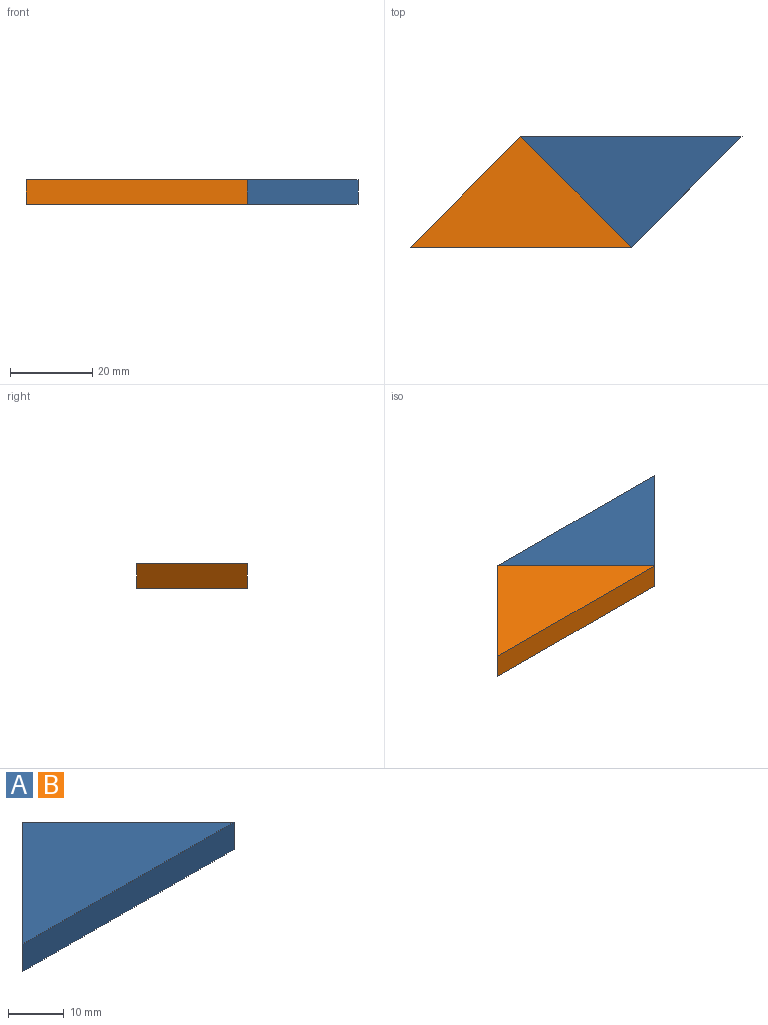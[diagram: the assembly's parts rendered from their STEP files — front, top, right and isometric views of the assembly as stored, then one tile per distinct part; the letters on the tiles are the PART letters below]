
ASSEMBLY  parts=2 mates=1
PART A: 5 faces, bbox 53.7x26.9x6 mm
  f0: plane 26.87x26.87mm, normal (-0.71,0.71,0), area 228mm2, adj f1,f2,f3,f4
  f1: plane 53.74x6mm, normal (0,-1,0), area 322.4mm2, adj f0,f2,f3,f4
  f2: plane 26.87x26.87mm, normal (0.71,0.71,0), area 228mm2, adj f0,f1,f3,f4
  f3: plane 53.74x26.87mm, normal (0,0,1), area 722mm2, adj f0,f1,f2
  f4: plane 53.74x26.87mm, normal (0,0,-1), area 722mm2, adj f0,f1,f2
PART B: same geometry as A
PLACE A rot(axis=(0,0,-1),180deg) t=(79.27,21.89,5.95)mm
PLACE B t=(-1.34,-4.98,5.95)mm
MATE fastened A.f2 <-> B.f2  axis (-0.71,-0.71,0) through (38.96,8.45,8.95)mm
